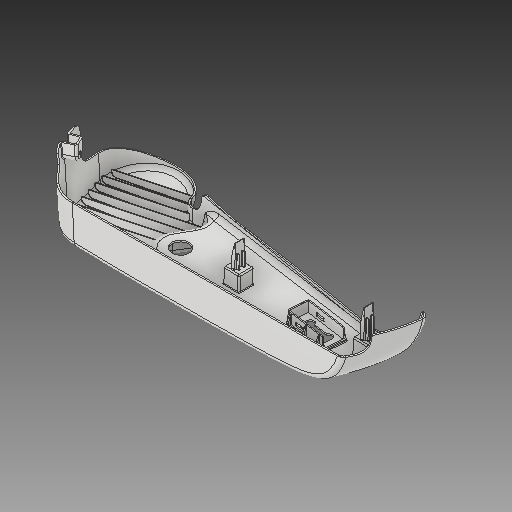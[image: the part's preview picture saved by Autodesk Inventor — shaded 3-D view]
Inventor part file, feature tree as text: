
AUTODESK INVENTOR PART (.ipt)
format: ipt  version: 2019 (Build 230136000, 136)  size: 9,529,856 bytes
history: native  units: in
note: dims shown in document units (in); Inventor stores cm internally (conversion verified against a paired STEP export)
features: other x46, sketch x14, plane x7
ambient origin geometry x8: Origin, YZ Plane, XZ Plane, XY Plane, X Axis, Y Axis, Z Axis, Center Point
bodies: Solid1 (feature_tree)
feature tree (67):
  other  "Side Cover.ipt"
  other  "Solid1::Side Cover.ipt"
  other  "TaggingFeature1"
  sketch  "Sketch1"  dims[d0=0.3937in]
  sketch  "Sketch2"
  sketch  "Sketch3"
  sketch  "Sketch4"
  sketch  "Sketch5"
  sketch  "Sketch6"
  sketch  "Sketch12"
  sketch  "Sketch14"
  sketch  "Sketch16"
  sketch  "Sketch17"
  sketch  "Sketch18"
  sketch  "Sketch19"
  sketch  "Sketch20"
  sketch  "Sketch21"
  plane  "Work Plane1"
  plane  "Work Plane2"
  plane  "Work Plane3"
  plane  "Work Plane4"
  plane  "Work Plane7"
  plane  "Work Plane8"
  plane  "Work Plane9"
  other  "Work Axis1"
  other  "Work Point1"
  other  "Work Point2"
  other  "Work Point3"
  other  "Work Point4"
  other  "Work Point5"
  other  "Work Point6"
  other  "Srf1"
  other  "Srf2"
  other  "Srf3"
  other  "Srf4"
  other  "Srf5"
  other  "Srf6"
  other  "Srf7"
  other  "Srf8"
  other  "Srf9"
  other  "Srf10"
  other  "Srf11"
  other  "Srf12"
  other  "Srf13"
  other  "Srf14"
  other  "Srf15"
  other  "Srf16"
  other  "Srf17"
  other  "Srf18"
  other  "Srf1::Derived"
  other  "Srf2::Derived"
  other  "Srf3::Derived"
  other  "Srf4::Derived"
  other  "Srf5::Derived"
  other  "Srf6::Derived"
  other  "Srf7::Derived"
  other  "Srf8::Derived"
  other  "Srf9::Derived"
  other  "Srf10::Derived"
  other  "Srf11::Derived"
  other  "Srf12::Derived"
  other  "Srf13::Derived"
  other  "Srf14::Derived"
  other  "Srf15::Derived"
  other  "Srf16::Derived"
  other  "Srf17::Derived"
  other  "Srf18::Derived"
